# Revit family: Legrand Accessoires Colonnes universelles
name_source: partatom
category: Installations électriques
units: mm (PartAtom-declared; Revit-internal decimal feet)

## family parameters
Conserver l'orientation des annotations = Non
Cote de connecteur circulaire = Utiliser le diamètre
Couper avec des vides une fois chargée = Non
Hôte = Face
Partagée = Non
Point de calcul de pièce = Non
Type d'élément = Normal

## types (4) — shared parameters
Fabricant = LEGRAND
Longueur CV = 80 mm  [stored 0.262467 ft]
Standard = Universelle

## per-type parameters (varying)
| type | Accessoire | Description | Elévation par défaut | Finition | Matériau principal | Modèle |
| Support signalétique | INFORMATIONS_PANEL_80 : 150x150mm | support signaletique 150x150mm avec interface cv80mm | 2000 mm  [stored 6.56168 ft] | Autre | Mixte | LG-653180 |
| Tablette | TABLES_80 | tablette support en corian Blanc pour Colonnes cv80mm - universelle | 900 mm  [stored 2.95276 ft] | Blanc | Corian | LG-653183 |
| Support écran 26 pouces | TV_SUPPORT_80 : 25-66cm | support ecran 10-26 pouces / 25-66cm / vesa. pour Colonne cv 80 | 1800 mm  [stored 5.90551 ft] | Autre | Mixte | LG-653181 |
| Support écran 42 pouces | TV_SUPPORT_80 : 66-107cm | support ecran 26-42 pouces / 66-107cm / vesa. pour Colonne cv 80 | 1800 mm  [stored 5.90551 ft] | Autre | Mixte | LG-653182 |

note: [stored X ft] marks values corroborated as IEEE doubles in the binary element streams (Revit-internal decimal feet)
